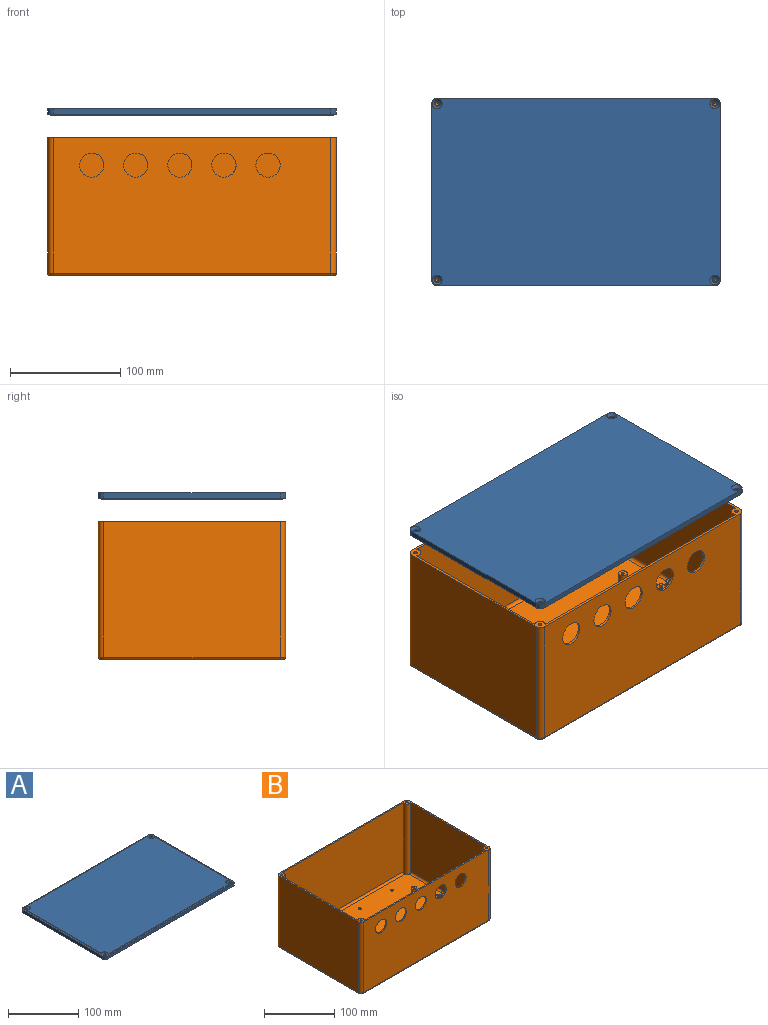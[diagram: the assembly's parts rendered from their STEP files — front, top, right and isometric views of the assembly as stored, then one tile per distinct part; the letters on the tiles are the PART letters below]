
ASSEMBLY  parts=2 mates=3
PART A: 27 faces, bbox 262x170x6 mm
  f0: plane 262x170mm, normal (0,0,1), area 2302.7mm2, adj f1,f2,f3,f4,f5,f6,f7,f8
  f1: plane 160x5mm, normal (1,0,0), area 800mm2, adj f0,f2,f8,f9
  f2: cylinder r=5mm len=5mm, axis (0,0,-1), area 39.3mm2, adj f0,f1,f3,f9
  f3: plane 252x5mm, normal (0,1,0), area 1260mm2, adj f0,f2,f4,f9
  f4: cylinder r=5mm len=5mm, axis (0,0,-1), area 39.3mm2, adj f0,f3,f5,f9
  f5: plane 160x5mm, normal (-1,0,0), area 800mm2, adj f0,f4,f6,f9
  f6: cylinder r=5mm len=5mm, axis (0,0,-1), area 39.3mm2, adj f0,f5,f7,f9
  f7: plane 252x5mm, normal (0,-1,0), area 1260mm2, adj f0,f6,f8,f9
  f8: cylinder r=5mm len=5mm, axis (0,0,-1), area 39.3mm2, adj f0,f1,f7,f9
  f9: plane 262x170mm, normal (0,0,-1), area 44266.3mm2, adj f1,f2,f3,f4,f5,f6,f7,f8
  f10: cylinder r=5mm len=8.93mm, axis (0,0,-1), area 15.6mm2, adj f0,f11,f17,f18
  f11: plane 243x1mm, normal (0,1,0), area 243mm2, adj f0,f10,f12,f18
  f12: cylinder r=5mm len=9.14mm, axis (0,0,-1), area 16.4mm2, adj f0,f11,f13,f18
  f13: plane 151x1mm, normal (-1,0,0), area 151mm2, adj f0,f12,f14,f18
  f14: cylinder r=5mm len=8.61mm, axis (0,0,-1), area 14.6mm2, adj f0,f13,f15,f18
  f15: plane 243x1mm, normal (0,-1,0), area 243mm2, adj f0,f14,f16,f18
  f16: cylinder r=5mm len=9.05mm, axis (0,0,-1), area 16mm2, adj f0,f15,f17,f18
  f17: plane 151x1mm, normal (1,0,0), area 151mm2, adj f0,f10,f16,f18
  f18: plane 257x165mm, normal (0,0,1), area 42152.2mm2, adj f10,f11,f12,f13,f14,f15,f16,f17
  f19: cylinder r=2.25mm len=4.5mm, axis (0,0,-1), area 39.2mm2, adj f0,f20
  f20: cone r=2.25mm half-angle=45deg, axis (0,0,-1), area 66.7mm2, adj f9,f19
  f21: cylinder r=2.25mm len=4.5mm, axis (0,0,-1), area 39.2mm2, adj f0,f22
  f22: cone r=2.25mm half-angle=45deg, axis (0,0,-1), area 66.7mm2, adj f9,f21
  f23: cylinder r=2.25mm len=4.5mm, axis (0,0,-1), area 39.2mm2, adj f0,f24
  f24: cone r=2.25mm half-angle=45deg, axis (0,0,-1), area 66.7mm2, adj f9,f23
  f25: cylinder r=2.25mm len=4.5mm, axis (0,0,-1), area 39.2mm2, adj f0,f26
  f26: cone r=2.25mm half-angle=45deg, axis (0,0,-1), area 66.7mm2, adj f9,f25
PART B: 70 faces, bbox 262.8x170.8x125 mm
  f0: plane 262x170mm, normal (0,0,1), area 1883.2mm2, adj f1,f2,f3,f4,f5,f6,f7,f8
  f1: plane 160x123mm, normal (1,0,0), area 19680mm2, adj f0,f2,f8,f48
  f2: cylinder r=5mm len=123mm, axis (0,0,-1), area 966mm2, adj f0,f1,f3,f50
  f3: plane 252x123mm, normal (0,1,0), area 30996mm2, adj f0,f2,f4,f49
  f4: cylinder r=5mm len=123mm, axis (0,0,-1), area 966mm2, adj f0,f3,f5,f47
  f5: plane 160x123mm, normal (-1,0,0), area 19680mm2, adj f0,f4,f6,f45
  f6: cylinder r=5mm len=123mm, axis (0,0,-1), area 966mm2, adj f0,f5,f7,f43
  f7: plane 252x123mm, normal (0,-1,0), area 29095.3mm2, adj f0,f6,f8,f44,f65,f66,f67,f68
  f8: cylinder r=5mm len=123mm, axis (0,0,-1), area 966mm2, adj f0,f1,f7,f46
  f9: plane 258x166mm, normal (0,0,-1), area 42656.3mm2, adj f35,f36,f37,f38,f39,f40,f41,f42
  f10: cylinder r=5mm len=123mm, axis (0,0,1), area 1753.1mm2, adj f0,f11,f17,f18,f21,f22
  f11: plane 244x120mm, normal (0,-1,0), area 29280mm2, adj f0,f10,f12,f21
  f12: cylinder r=5mm len=123mm, axis (0,0,1), area 1753.1mm2, adj f0,f11,f13,f18,f20,f21
  f13: plane 152x120mm, normal (1,0,0), area 18240mm2, adj f0,f12,f14,f20
  f14: cylinder r=5mm len=123mm, axis (0,0,1), area 1753.1mm2, adj f0,f13,f15,f18,f19,f20
  f15: plane 244x120mm, normal (0,1,0), area 27379.3mm2, adj f0,f14,f16,f19,f65,f66,f67,f68
  f16: cylinder r=5mm len=123mm, axis (0,0,1), area 1753.1mm2, adj f0,f15,f17,f18,f19,f22
  f17: plane 152x120mm, normal (-1,0,0), area 18240mm2, adj f0,f10,f16,f22
  f18: plane 252x160mm, normal (0,0,1), area 39812.6mm2, adj f10,f12,f14,f16,f19,f20,f21,f22
  f19: cylinder r=3mm len=244mm, axis (1,0,0), area 1145mm2, adj f14,f15,f16,f18
  f20: cylinder r=3mm len=152mm, axis (0,-1,0), area 711.4mm2, adj f12,f13,f14,f18
  f21: cylinder r=3mm len=244mm, axis (-1,0,0), area 1145mm2, adj f10,f11,f12,f18
  f22: cylinder r=3mm len=152mm, axis (0,1,0), area 711.4mm2, adj f10,f16,f17,f18
  f23: cylinder r=4mm len=8mm, axis (0,0,-1), area 201.1mm2, adj f18,f24
  f24: plane 8x8mm, normal (0,0,1), area 41.7mm2, adj f23,f56
  f25: cylinder r=4mm len=8mm, axis (0,0,-1), area 201.1mm2, adj f18,f26
  f26: plane 8x8mm, normal (0,0,1), area 41.7mm2, adj f25,f55
  f27: cylinder r=4mm len=8mm, axis (0,0,-1), area 201.1mm2, adj f18,f28
  f28: plane 8x8mm, normal (0,0,1), area 45.4mm2, adj f27,f54
  f29: cylinder r=4mm len=8mm, axis (0,0,-1), area 201.1mm2, adj f18,f30
  f30: plane 8x8mm, normal (0,0,1), area 45.4mm2, adj f29,f53
  f31: cylinder r=4mm len=8mm, axis (0,0,-1), area 201.1mm2, adj f18,f32
  f32: plane 8x8mm, normal (0,0,1), area 45.4mm2, adj f31,f52
  f33: cylinder r=4mm len=8mm, axis (0,0,-1), area 201.1mm2, adj f18,f34
  f34: plane 8x8mm, normal (0,0,1), area 45.4mm2, adj f33,f51
  f35: cylinder r=2.25mm len=4.5mm, axis (0,0,1), area 28.3mm2, adj f9,f18
  f36: cylinder r=2.25mm len=4.5mm, axis (0,0,1), area 28.3mm2, adj f9,f18
  f37: cylinder r=2.25mm len=4.5mm, axis (0,0,1), area 28.3mm2, adj f9,f18
  f38: cylinder r=2.25mm len=4.5mm, axis (0,0,1), area 28.3mm2, adj f9,f18
  f39: cylinder r=2.25mm len=4.5mm, axis (0,0,1), area 28.3mm2, adj f9,f18
  f40: cylinder r=2.25mm len=4.5mm, axis (0,0,1), area 28.3mm2, adj f9,f18
  f41: cylinder r=2.25mm len=4.5mm, axis (0,0,1), area 28.3mm2, adj f9,f18
  f42: cylinder r=2.25mm len=4.5mm, axis (0,0,1), area 28.3mm2, adj f9,f18
  f43: torus R=3mm, axis (0,0,1), area 21.1mm2, adj f6,f9,f44,f45
  f44: cylinder r=2mm len=252mm, axis (1,0,0), area 791.7mm2, adj f7,f9,f43,f46
  f45: cylinder r=2mm len=160mm, axis (0,-1,0), area 502.7mm2, adj f5,f9,f43,f47
  f46: torus R=3mm, axis (0,0,1), area 21.1mm2, adj f8,f9,f44,f48
  f47: torus R=3mm, axis (0,0,1), area 21.1mm2, adj f4,f9,f45,f49
  f48: cylinder r=2mm len=160mm, axis (0,1,0), area 502.7mm2, adj f1,f9,f46,f50
  f49: cylinder r=2mm len=252mm, axis (-1,0,0), area 791.7mm2, adj f3,f9,f47,f50
  f50: torus R=3mm, axis (0,0,1), area 21.1mm2, adj f2,f9,f48,f49
  f51: cylinder r=1.25mm len=10mm, axis (0,0,1), area 78.5mm2, adj f9,f34
  f52: cylinder r=1.25mm len=10mm, axis (0,0,1), area 78.5mm2, adj f9,f32
  f53: cylinder r=1.25mm len=10mm, axis (0,0,1), area 78.5mm2, adj f9,f30
  f54: cylinder r=1.25mm len=10mm, axis (0,0,1), area 78.5mm2, adj f9,f28
  f55: cylinder r=1.65mm len=10mm, axis (0,0,1), area 103.7mm2, adj f9,f26
  f56: cylinder r=1.65mm len=10mm, axis (0,0,1), area 103.7mm2, adj f9,f24
  f57: cone r=0mm half-angle=59deg, axis (0,0,1), area 10mm2, adj f58
  f58: cylinder r=1.65mm len=19.1mm, axis (0,0,1), area 198mm2, adj f0,f57
  f59: cone r=0mm half-angle=59deg, axis (0,0,1), area 10mm2, adj f60
  f60: cylinder r=1.65mm len=19.1mm, axis (0,0,1), area 198mm2, adj f0,f59
  f61: cone r=0mm half-angle=59deg, axis (0,0,1), area 10mm2, adj f62
  f62: cylinder r=1.65mm len=19.1mm, axis (0,0,1), area 198mm2, adj f0,f61
  f63: cone r=0mm half-angle=59deg, axis (0,0,1), area 10mm2, adj f64
  f64: cylinder r=1.65mm len=19.1mm, axis (0,0,1), area 198mm2, adj f0,f63
  f65: cylinder r=11mm len=22mm, axis (0,-1,0), area 138.2mm2, adj f7,f15
  f66: cylinder r=11mm len=22mm, axis (0,-1,0), area 138.2mm2, adj f7,f15
  f67: cylinder r=11mm len=22mm, axis (0,-1,0), area 138.2mm2, adj f7,f15
  f68: cylinder r=11mm len=22mm, axis (0,-1,0), area 138.2mm2, adj f7,f15
  f69: cylinder r=11mm len=22mm, axis (0,-1,0), area 138.2mm2, adj f7,f15
PLACE A rot(axis=(1,0,0),180deg) t=(204.29,238.77,146.14)mm
PLACE B t=(31.34,128.28,-5.03)mm
MATE parallel A.f18 <-> B.f18  axis (0,0,-1) through (162.33,213.3,140.14)mm
MATE planar A.f3 <-> B.f7  axis (0,-1,0) through (162.34,128.28,143.64)mm
MATE planar A.f1 <-> B.f1  axis (1,0,0) through (293.34,213.28,143.64)mm
